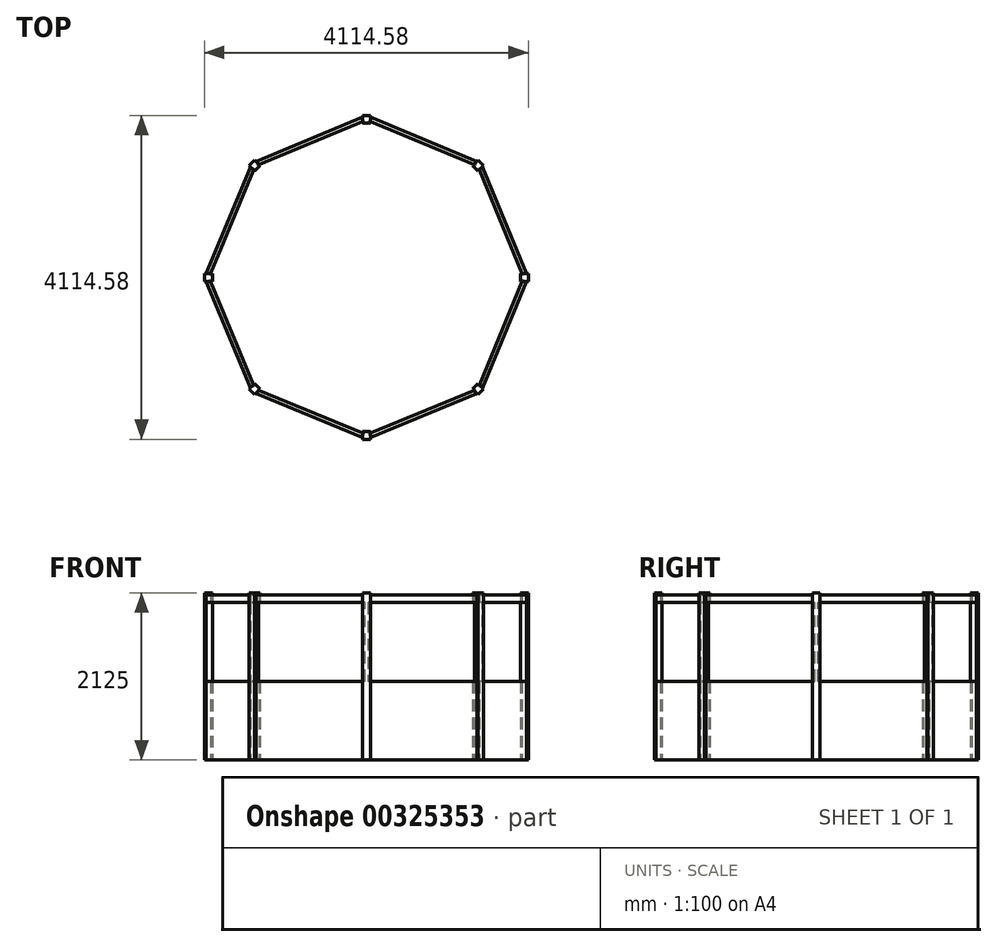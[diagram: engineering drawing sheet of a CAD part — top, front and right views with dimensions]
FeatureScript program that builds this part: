
annotation { "Feature Type Name" : "Feature", "Feature Type Description" : "" }
export const myFeature = defineFeature(function(context is Context, id is Id, definition is map)
    precondition{}
    {
        {
            var Q0;
            Q0=qCreatedBy(makeId("Top.planeOp"),FACE);
            var sketch = newSketch(context, id + "F0", { "sketchPlane" : qUnion([Q0])});
            skCircle(sketch, "E0.cCircle", {"center": v(0, 0) * mm, "radius": 1847.76 * mm, "construction": true});
            skLineSegment(sketch, "E0.0", {"start": v(2000, 0) * mm, "end": v(1414.21, -1414.21) * mm});
            skLineSegment(sketch, "E0.1", {"start": v(1414.21, -1414.21) * mm, "end": v(0, -2000) * mm});
            skLineSegment(sketch, "E0.2", {"start": v(0, -2000) * mm, "end": v(-1414.21, -1414.21) * mm});
            skLineSegment(sketch, "E0.3", {"start": v(-1414.21, -1414.21) * mm, "end": v(-2000, 0) * mm});
            skLineSegment(sketch, "E0.4", {"start": v(-2000, 0) * mm, "end": v(-1414.21, 1414.21) * mm});
            skLineSegment(sketch, "E0.5", {"start": v(-1414.21, 1414.21) * mm, "end": v(0, 2000) * mm});
            skLineSegment(sketch, "E0.6", {"start": v(0, 2000) * mm, "end": v(1414.21, 1414.21) * mm});
            skLineSegment(sketch, "E0.7", {"start": v(1414.21, 1414.21) * mm, "end": v(2000, 0) * mm});
            skPoint(sketch, "E0.0.midPoint", {"position": v(1707.1, -707.1) * mm});
            skPoint(sketch, "E1.middle", {"position": v(1414.21, -1414.21) * mm});
            skPoint(sketch, "E2.middle", {"position": v(2000, 0) * mm});
            skLineSegment(sketch, "E3", {"start": v(2017.31, -91.48) * mm, "end": v(2055.2, 0) * mm});
            skPoint(sketch, "E4.end.orphan", {"position": v(1956.9, 0) * mm});
            skPoint(sketch, "E5.end.orphan", {"position": v(2050, 0) * mm});
            skLineSegment(sketch, "E6.0", {"start": v(-1453.25, 1453.25) * mm, "end": v(0, 2055.2) * mm});
            skLineSegment(sketch, "E6.1", {"start": v(-2055.2, 0) * mm, "end": v(-1453.25, 1453.25) * mm});
            skLineSegment(sketch, "E6.2", {"start": v(0, 2055.2) * mm, "end": v(1453.25, 1453.25) * mm});
            skLineSegment(sketch, "E6.3", {"start": v(-1453.25, -1453.25) * mm, "end": v(-2055.2, 0) * mm});
            skLineSegment(sketch, "E6.4", {"start": v(1453.25, 1453.25) * mm, "end": v(2055.2, 0) * mm});
            skLineSegment(sketch, "E6.5", {"start": v(2055.2, 0) * mm, "end": v(1453.25, -1453.25) * mm});
            skLineSegment(sketch, "E6.6", {"start": v(1453.25, -1453.25) * mm, "end": v(0, -2055.2) * mm});
            skLineSegment(sketch, "E6.7", {"start": v(0, -2055.2) * mm, "end": v(-1453.25, -1453.25) * mm});
            skLineSegment(sketch, "E7", {"start": v(0, 2754.8) * mm, "end": v(0, -3839.53) * mm});
            skLineSegment(sketch, "E8", {"start": v(-2590.03, 0) * mm, "end": v(5183.87, 0) * mm});
            skLineSegment(sketch, "E9", {"start": v(2000, 0) * mm, "end": v(0, -2000) * mm});
            skLineSegment(sketch, "E10", {"start": v(0, 0) * mm, "end": v(1464.21, -1464.21) * mm});
            skLineSegment(sketch, "E11", {"start": v(0, -2055.2) * mm, "end": v(0, -2000) * mm});
            skPoint(sketch, "E12.middle", {"position": v(0, -2027.6) * mm});
            skLineSegment(sketch, "E13", {"start": v(-50, -1957.29) * mm, "end": v(-50, -2057.29) * mm});
            skLineSegment(sketch, "E14", {"start": v(50, -1957.29) * mm, "end": v(50, -2057.29) * mm});
            skLineSegment(sketch, "E15", {"start": v(-50, -1957.29) * mm, "end": v(50, -1957.29) * mm});
            skLineSegment(sketch, "E16", {"start": v(-50, -2057.29) * mm, "end": v(50, -2057.29) * mm});
            skLineSegment(sketch, "E17", {"start": v(-50, -1979.29) * mm, "end": v(50, -1979.29) * mm});
            skPoint(sketch, "E18.endSnap0", {"position": v(0, -1979.29) * mm});
            skLineSegment(sketch, "E19", {"start": v(-50, -2034.5) * mm, "end": v(50, -2034.5) * mm});
            skPoint(sketch, "E20.orphan", {"position": v(-81.67, -1979.29) * mm});
            skPoint(sketch, "E21.orphan", {"position": v(96.93, -1979.29) * mm});
            skLineSegment(sketch, "E22.1.0", {"start": v(1348.66, -1419.37) * mm, "end": v(1419.37, -1348.66) * mm});
            skLineSegment(sketch, "E22.1.1", {"start": v(1419.37, -1348.66) * mm, "end": v(1490.08, -1419.37) * mm});
            skLineSegment(sketch, "E22.1.2", {"start": v(1419.37, -1490.08) * mm, "end": v(1490.08, -1419.37) * mm});
            skLineSegment(sketch, "E22.1.3", {"start": v(1348.66, -1419.37) * mm, "end": v(1419.37, -1490.08) * mm});
            skLineSegment(sketch, "E22.anchor1", {"start": v(0, 0) * mm, "end": v(-50, -1957.29) * mm, "construction": true});
            skLineSegment(sketch, "E22.anchor2", {"start": v(0, 0) * mm, "end": v(-1419.37, -1348.66) * mm, "construction": true});
            skLineSegment(sketch, "E23.1.2.0", {"start": v(1957.29, -50) * mm, "end": v(1957.29, 50) * mm});
            skLineSegment(sketch, "E23.3.2.0", {"start": v(1957.29, 50) * mm, "end": v(2057.29, 50) * mm});
            skLineSegment(sketch, "E23.6.2.0", {"start": v(2057.29, -50) * mm, "end": v(2057.29, 50) * mm});
            skLineSegment(sketch, "E23.9.2.0", {"start": v(1957.29, -50) * mm, "end": v(2057.29, -50) * mm});
            skLineSegment(sketch, "E23.1.3.0", {"start": v(1419.37, 1348.66) * mm, "end": v(1348.66, 1419.37) * mm});
            skLineSegment(sketch, "E23.3.3.0", {"start": v(1348.66, 1419.37) * mm, "end": v(1419.37, 1490.08) * mm});
            skLineSegment(sketch, "E23.6.3.0", {"start": v(1490.08, 1419.37) * mm, "end": v(1419.37, 1490.08) * mm});
            skLineSegment(sketch, "E23.9.3.0", {"start": v(1419.37, 1348.66) * mm, "end": v(1490.08, 1419.37) * mm});
            skLineSegment(sketch, "E23.1.4.0", {"start": v(50, 1957.29) * mm, "end": v(-50, 1957.29) * mm});
            skLineSegment(sketch, "E23.3.4.0", {"start": v(-50, 1957.29) * mm, "end": v(-50, 2057.29) * mm});
            skLineSegment(sketch, "E23.6.4.0", {"start": v(50, 2057.29) * mm, "end": v(-50, 2057.29) * mm});
            skLineSegment(sketch, "E23.9.4.0", {"start": v(50, 1957.29) * mm, "end": v(50, 2057.29) * mm});
            skLineSegment(sketch, "E23.1.5.0", {"start": v(-1348.66, 1419.37) * mm, "end": v(-1419.37, 1348.66) * mm});
            skLineSegment(sketch, "E23.3.5.0", {"start": v(-1419.37, 1348.66) * mm, "end": v(-1490.08, 1419.37) * mm});
            skLineSegment(sketch, "E23.6.5.0", {"start": v(-1419.37, 1490.08) * mm, "end": v(-1490.08, 1419.37) * mm});
            skLineSegment(sketch, "E23.9.5.0", {"start": v(-1348.66, 1419.37) * mm, "end": v(-1419.37, 1490.08) * mm});
            skLineSegment(sketch, "E23.1.6.0", {"start": v(-1957.29, 50) * mm, "end": v(-1957.29, -50) * mm});
            skLineSegment(sketch, "E23.3.6.0", {"start": v(-1957.29, -50) * mm, "end": v(-2057.29, -50) * mm});
            skLineSegment(sketch, "E23.6.6.0", {"start": v(-2057.29, 50) * mm, "end": v(-2057.29, -50) * mm});
            skLineSegment(sketch, "E23.9.6.0", {"start": v(-1957.29, 50) * mm, "end": v(-2057.29, 50) * mm});
            skLineSegment(sketch, "E23.1.7.0", {"start": v(-1419.37, -1348.66) * mm, "end": v(-1348.66, -1419.37) * mm});
            skLineSegment(sketch, "E23.3.7.0", {"start": v(-1348.66, -1419.37) * mm, "end": v(-1419.37, -1490.08) * mm});
            skLineSegment(sketch, "E23.6.7.0", {"start": v(-1490.08, -1419.37) * mm, "end": v(-1419.37, -1490.08) * mm});
            skLineSegment(sketch, "E23.9.7.0", {"start": v(-1419.37, -1348.66) * mm, "end": v(-1490.08, -1419.37) * mm});
            skSolve(sketch);
        }
        {
            var Q0;
            {var subQ3=sQuery(id+"F0.wireOp",EDGE,"E14");var subQ5=sQuery(id+"F0.wireOp",EDGE,"E16");var subQ7=makeQuery(id+"F0.imprint","INTERSECT",VERTEX,{"derivedFrom":[subQ3,subQ5]});Q0=makeQuery(id+"F0.imprint","IMPRINT",FACE,{"disambiguationData":[TD([[makeQuery(id+"F0.imprint","IMPRINT",EDGE,{"disambiguationData":[TD([[subQ7,1.0]])],"derivedFrom":subQ5}),1.0]])]});}
            var Q1;
            {var subQ0=sQuery(id+"F0.wireOp",EDGE,"E11");var subQ3=sQuery(id+"F0.wireOp",EDGE,"E19");var subQ5=makeQuery(id+"F0.imprint","INTERSECT",VERTEX,{"derivedFrom":[subQ0,subQ3]});Q1=makeQuery(id+"F0.imprint","IMPRINT",FACE,{"disambiguationData":[TD([[makeQuery(id+"F0.imprint","IMPRINT",EDGE,{"disambiguationData":[TD([[subQ5,-1.0]])],"derivedFrom":subQ3}),-1.0]])]});}
            var Q2;
            {var subQ0=sQuery(id+"F0.wireOp",EDGE,"E11");var subQ3=sQuery(id+"F0.wireOp",EDGE,"E19");var subQ5=makeQuery(id+"F0.imprint","INTERSECT",VERTEX,{"derivedFrom":[subQ0,subQ3]});Q2=makeQuery(id+"F0.imprint","IMPRINT",FACE,{"disambiguationData":[TD([[makeQuery(id+"F0.imprint","IMPRINT",EDGE,{"disambiguationData":[TD([[subQ5,1.0]])],"derivedFrom":subQ3}),-1.0]])]});}
            var Q3;
            {var subQ3=sQuery(id+"F0.wireOp",EDGE,"E13");var subQ5=sQuery(id+"F0.wireOp",EDGE,"E16");var subQ7=makeQuery(id+"F0.imprint","INTERSECT",VERTEX,{"derivedFrom":[subQ3,subQ5]});Q3=makeQuery(id+"F0.imprint","IMPRINT",FACE,{"disambiguationData":[TD([[makeQuery(id+"F0.imprint","IMPRINT",EDGE,{"disambiguationData":[TD([[subQ7,-1.0]])],"derivedFrom":subQ5}),1.0]])]});}
            var Q4;
            {var subQ0=sQuery(id+"F0.wireOp",EDGE,"E11");var subQ5=sQuery(id+"F0.wireOp",EDGE,"E19");var subQ6=makeQuery(id+"F0.imprint","INTERSECT",VERTEX,{"derivedFrom":[subQ0,subQ5]});Q4=makeQuery(id+"F0.imprint","IMPRINT",FACE,{"disambiguationData":[TD([[makeQuery(id+"F0.imprint","IMPRINT",EDGE,{"disambiguationData":[TD([[subQ6,1.0]])],"derivedFrom":subQ5}),1.0]])]});}
            var Q5;
            {var subQ0=sQuery(id+"F0.wireOp",EDGE,"E11");var subQ5=sQuery(id+"F0.wireOp",EDGE,"E19");var subQ6=makeQuery(id+"F0.imprint","INTERSECT",VERTEX,{"derivedFrom":[subQ0,subQ5]});Q5=makeQuery(id+"F0.imprint","IMPRINT",FACE,{"disambiguationData":[TD([[makeQuery(id+"F0.imprint","IMPRINT",EDGE,{"disambiguationData":[TD([[subQ6,-1.0]])],"derivedFrom":subQ5}),1.0]])]});}
            var Q6;
            {var subQ0=sQuery(id+"F0.wireOp",EDGE,"E9");var subQ3=sQuery(id+"F0.wireOp",EDGE,"E17");var subQ5=makeQuery(id+"F0.imprint","INTERSECT",VERTEX,{"derivedFrom":[subQ0,subQ3]});Q6=makeQuery(id+"F0.imprint","IMPRINT",FACE,{"disambiguationData":[TD([[makeQuery(id+"F0.imprint","IMPRINT",EDGE,{"disambiguationData":[TD([[subQ5,-1.0]])],"derivedFrom":subQ3}),-1.0]])]});}
            var Q7;
            {var subQ1=sQuery(id+"F0.wireOp",EDGE,"E7");var subQ3=sQuery(id+"F0.wireOp",EDGE,"E17");var subQ4=makeQuery(id+"F0.imprint","INTERSECT",VERTEX,{"derivedFrom":[subQ1,subQ3]});Q7=makeQuery(id+"F0.imprint","IMPRINT",FACE,{"disambiguationData":[TD([[makeQuery(id+"F0.imprint","IMPRINT",EDGE,{"disambiguationData":[TD([[subQ4,-1.0]])],"derivedFrom":subQ3}),-1.0]])]});}
            var Q8;
            {var subQ0=sQuery(id+"F0.wireOp",EDGE,"E7");var subQ3=sQuery(id+"F0.wireOp",EDGE,"E17");var subQ5=makeQuery(id+"F0.imprint","INTERSECT",VERTEX,{"derivedFrom":[subQ0,subQ3]});Q8=makeQuery(id+"F0.imprint","IMPRINT",FACE,{"disambiguationData":[TD([[makeQuery(id+"F0.imprint","IMPRINT",EDGE,{"disambiguationData":[TD([[subQ5,1.0]])],"derivedFrom":subQ3}),-1.0]])]});}
            var Q9;
            {var subQ0=sQuery(id+"F0.wireOp",EDGE,"E15");var subQ1=sQuery(id+"F0.wireOp",EDGE,"E7");var subQ2=makeQuery(id+"F0.imprint","INTERSECT",VERTEX,{"derivedFrom":[subQ1,subQ0]});Q9=makeQuery(id+"F0.imprint","IMPRINT",FACE,{"disambiguationData":[TD([[makeQuery(id+"F0.imprint","IMPRINT",EDGE,{"disambiguationData":[TD([[subQ2,-1.0]])],"derivedFrom":subQ1}),-1.0]])]});}
            var Q10;
            {var subQ0=sQuery(id+"F0.wireOp",EDGE,"E15");var subQ1=sQuery(id+"F0.wireOp",EDGE,"E7");var subQ2=makeQuery(id+"F0.imprint","INTERSECT",VERTEX,{"derivedFrom":[subQ1,subQ0]});Q10=makeQuery(id+"F0.imprint","IMPRINT",FACE,{"disambiguationData":[TD([[makeQuery(id+"F0.imprint","IMPRINT",EDGE,{"disambiguationData":[TD([[subQ2,-1.0]])],"derivedFrom":subQ1}),1.0]])]});}
            var Q11;
            {var subQ0=sQuery(id+"F0.wireOp",EDGE,"E15");var subQ1=sQuery(id+"F0.wireOp",EDGE,"E9");var subQ2=makeQuery(id+"F0.imprint","INTERSECT",VERTEX,{"derivedFrom":[subQ1,subQ0]});Q11=makeQuery(id+"F0.imprint","IMPRINT",FACE,{"disambiguationData":[TD([[makeQuery(id+"F0.imprint","IMPRINT",EDGE,{"disambiguationData":[TD([[subQ2,-1.0]])],"derivedFrom":subQ1}),1.0]])]});}
            var Q12;
            {var subQ0=sQuery(id+"F0.wireOp",EDGE,"E23.6.7.0");Q12=makeQuery(id+"F0.imprint","IMPRINT",FACE,{"disambiguationData":[TD([[makeQuery(id+"F0.imprint","IMPRINT",EDGE,{"derivedFrom":subQ0}),1.0]])]});}
            var Q13;
            {var subQ5=sQuery(id+"F0.wireOp",EDGE,"E0.3");var subQ6=sQuery(id+"F0.wireOp",EDGE,"E0.2");var subQ7=makeQuery(id+"F0.imprint","INTERSECT",VERTEX,{"derivedFrom":[subQ6,subQ5]});Q13=makeQuery(id+"F0.imprint","IMPRINT",FACE,{"disambiguationData":[TD([[makeQuery(id+"F0.imprint","IMPRINT",EDGE,{"disambiguationData":[TD([[subQ7,1.0]])],"derivedFrom":subQ6}),1.0]])]});}
            var Q14;
            {var subQ1=sQuery(id+"F0.wireOp",EDGE,"E23.1.7.0");Q14=makeQuery(id+"F0.imprint","IMPRINT",FACE,{"disambiguationData":[TD([[makeQuery(id+"F0.imprint","IMPRINT",EDGE,{"derivedFrom":subQ1}),-1.0]])]});}
            var Q15;
            {var subQ3=sQuery(id+"F0.wireOp",EDGE,"E23.3.6.0");var subQ5=sQuery(id+"F0.wireOp",EDGE,"E6.3");var subQ7=makeQuery(id+"F0.imprint","INTERSECT",VERTEX,{"derivedFrom":[subQ5,subQ3]});Q15=makeQuery(id+"F0.imprint","IMPRINT",FACE,{"disambiguationData":[TD([[makeQuery(id+"F0.imprint","IMPRINT",EDGE,{"disambiguationData":[TD([[subQ7,1.0]])],"derivedFrom":subQ3}),-1.0]])]});}
            var Q16;
            {var subQ3=sQuery(id+"F0.wireOp",EDGE,"E23.3.6.0");var subQ5=sQuery(id+"F0.wireOp",EDGE,"E23.6.6.0");var subQ6=makeQuery(id+"F0.imprint","INTERSECT",VERTEX,{"derivedFrom":[subQ3,subQ5]});Q16=makeQuery(id+"F0.imprint","IMPRINT",FACE,{"disambiguationData":[TD([[makeQuery(id+"F0.imprint","IMPRINT",EDGE,{"disambiguationData":[TD([[subQ6,1.0]])],"derivedFrom":subQ3}),-1.0]])]});}
            var Q17;
            {var subQ3=sQuery(id+"F0.wireOp",EDGE,"E23.9.6.0");var subQ5=sQuery(id+"F0.wireOp",EDGE,"E23.6.6.0");var subQ7=makeQuery(id+"F0.imprint","INTERSECT",VERTEX,{"derivedFrom":[subQ5,subQ3]});Q17=makeQuery(id+"F0.imprint","IMPRINT",FACE,{"disambiguationData":[TD([[makeQuery(id+"F0.imprint","IMPRINT",EDGE,{"disambiguationData":[TD([[subQ7,-1.0]])],"derivedFrom":subQ5}),1.0]])]});}
            var Q18;
            {var subQ3=sQuery(id+"F0.wireOp",EDGE,"E23.9.6.0");var subQ5=sQuery(id+"F0.wireOp",EDGE,"E6.1");var subQ7=makeQuery(id+"F0.imprint","INTERSECT",VERTEX,{"derivedFrom":[subQ5,subQ3]});Q18=makeQuery(id+"F0.imprint","IMPRINT",FACE,{"disambiguationData":[TD([[makeQuery(id+"F0.imprint","IMPRINT",EDGE,{"disambiguationData":[TD([[subQ7,1.0]])],"derivedFrom":subQ3}),1.0]])]});}
            var Q19;
            {var subQ3=sQuery(id+"F0.wireOp",EDGE,"E23.9.6.0");var subQ5=sQuery(id+"F0.wireOp",EDGE,"E23.1.6.0");var subQ7=makeQuery(id+"F0.imprint","INTERSECT",VERTEX,{"derivedFrom":[subQ5,subQ3]});Q19=makeQuery(id+"F0.imprint","IMPRINT",FACE,{"disambiguationData":[TD([[makeQuery(id+"F0.imprint","IMPRINT",EDGE,{"disambiguationData":[TD([[subQ7,-1.0]])],"derivedFrom":subQ5}),-1.0]])]});}
            var Q20;
            {var subQ3=sQuery(id+"F0.wireOp",EDGE,"E23.3.6.0");var subQ5=sQuery(id+"F0.wireOp",EDGE,"E23.1.6.0");var subQ6=makeQuery(id+"F0.imprint","INTERSECT",VERTEX,{"derivedFrom":[subQ5,subQ3]});Q20=makeQuery(id+"F0.imprint","IMPRINT",FACE,{"disambiguationData":[TD([[makeQuery(id+"F0.imprint","IMPRINT",EDGE,{"disambiguationData":[TD([[subQ6,1.0]])],"derivedFrom":subQ5}),-1.0]])]});}
            var Q21;
            {var subQ1=sQuery(id+"F0.wireOp",EDGE,"E23.1.5.0");Q21=makeQuery(id+"F0.imprint","IMPRINT",FACE,{"disambiguationData":[TD([[makeQuery(id+"F0.imprint","IMPRINT",EDGE,{"derivedFrom":subQ1}),-1.0]])]});}
            var Q22;
            {var subQ0=sQuery(id+"F0.wireOp",EDGE,"E0.5");var subQ1=sQuery(id+"F0.wireOp",EDGE,"E0.4");var subQ2=makeQuery(id+"F0.imprint","INTERSECT",VERTEX,{"derivedFrom":[subQ1,subQ0]});Q22=makeQuery(id+"F0.imprint","IMPRINT",FACE,{"disambiguationData":[TD([[makeQuery(id+"F0.imprint","IMPRINT",EDGE,{"disambiguationData":[TD([[subQ2,1.0]])],"derivedFrom":subQ1}),1.0]])]});}
            var Q23;
            {var subQ0=sQuery(id+"F0.wireOp",EDGE,"E23.6.5.0");Q23=makeQuery(id+"F0.imprint","IMPRINT",FACE,{"disambiguationData":[TD([[makeQuery(id+"F0.imprint","IMPRINT",EDGE,{"derivedFrom":subQ0}),1.0]])]});}
            var Q24;
            {var subQ3=sQuery(id+"F0.wireOp",EDGE,"E23.9.4.0");var subQ5=sQuery(id+"F0.wireOp",EDGE,"E23.1.4.0");var subQ6=makeQuery(id+"F0.imprint","INTERSECT",VERTEX,{"derivedFrom":[subQ5,subQ3]});Q24=makeQuery(id+"F0.imprint","IMPRINT",FACE,{"disambiguationData":[TD([[makeQuery(id+"F0.imprint","IMPRINT",EDGE,{"disambiguationData":[TD([[subQ6,-1.0]])],"derivedFrom":subQ5}),-1.0]])]});}
            var Q25;
            {var subQ3=sQuery(id+"F0.wireOp",EDGE,"E23.3.4.0");var subQ5=sQuery(id+"F0.wireOp",EDGE,"E23.1.4.0");var subQ6=makeQuery(id+"F0.imprint","INTERSECT",VERTEX,{"derivedFrom":[subQ5,subQ3]});Q25=makeQuery(id+"F0.imprint","IMPRINT",FACE,{"disambiguationData":[TD([[makeQuery(id+"F0.imprint","IMPRINT",EDGE,{"disambiguationData":[TD([[subQ6,1.0]])],"derivedFrom":subQ5}),-1.0]])]});}
            var Q26;
            {var subQ3=sQuery(id+"F0.wireOp",EDGE,"E23.3.4.0");var subQ5=sQuery(id+"F0.wireOp",EDGE,"E6.0");var subQ7=makeQuery(id+"F0.imprint","INTERSECT",VERTEX,{"derivedFrom":[subQ5,subQ3]});Q26=makeQuery(id+"F0.imprint","IMPRINT",FACE,{"disambiguationData":[TD([[makeQuery(id+"F0.imprint","IMPRINT",EDGE,{"disambiguationData":[TD([[subQ7,1.0]])],"derivedFrom":subQ3}),-1.0]])]});}
            var Q27;
            {var subQ3=sQuery(id+"F0.wireOp",EDGE,"E23.9.4.0");var subQ5=sQuery(id+"F0.wireOp",EDGE,"E6.2");var subQ7=makeQuery(id+"F0.imprint","INTERSECT",VERTEX,{"derivedFrom":[subQ5,subQ3]});Q27=makeQuery(id+"F0.imprint","IMPRINT",FACE,{"disambiguationData":[TD([[makeQuery(id+"F0.imprint","IMPRINT",EDGE,{"disambiguationData":[TD([[subQ7,1.0]])],"derivedFrom":subQ3}),1.0]])]});}
            var Q28;
            {var subQ3=sQuery(id+"F0.wireOp",EDGE,"E23.9.4.0");var subQ5=sQuery(id+"F0.wireOp",EDGE,"E23.6.4.0");var subQ6=makeQuery(id+"F0.imprint","INTERSECT",VERTEX,{"derivedFrom":[subQ5,subQ3]});Q28=makeQuery(id+"F0.imprint","IMPRINT",FACE,{"disambiguationData":[TD([[makeQuery(id+"F0.imprint","IMPRINT",EDGE,{"disambiguationData":[TD([[subQ6,-1.0]])],"derivedFrom":subQ5}),1.0]])]});}
            var Q29;
            {var subQ3=sQuery(id+"F0.wireOp",EDGE,"E23.3.4.0");var subQ5=sQuery(id+"F0.wireOp",EDGE,"E23.6.4.0");var subQ7=makeQuery(id+"F0.imprint","INTERSECT",VERTEX,{"derivedFrom":[subQ3,subQ5]});Q29=makeQuery(id+"F0.imprint","IMPRINT",FACE,{"disambiguationData":[TD([[makeQuery(id+"F0.imprint","IMPRINT",EDGE,{"disambiguationData":[TD([[subQ7,1.0]])],"derivedFrom":subQ3}),-1.0]])]});}
            var Q30;
            {var subQ0=sQuery(id+"F0.wireOp",EDGE,"E23.6.3.0");Q30=makeQuery(id+"F0.imprint","IMPRINT",FACE,{"disambiguationData":[TD([[makeQuery(id+"F0.imprint","IMPRINT",EDGE,{"derivedFrom":subQ0}),1.0]])]});}
            var Q31;
            {var subQ5=sQuery(id+"F0.wireOp",EDGE,"E0.7");var subQ6=sQuery(id+"F0.wireOp",EDGE,"E0.6");var subQ7=makeQuery(id+"F0.imprint","INTERSECT",VERTEX,{"derivedFrom":[subQ6,subQ5]});Q31=makeQuery(id+"F0.imprint","IMPRINT",FACE,{"disambiguationData":[TD([[makeQuery(id+"F0.imprint","IMPRINT",EDGE,{"disambiguationData":[TD([[subQ7,1.0]])],"derivedFrom":subQ6}),1.0]])]});}
            var Q32;
            {var subQ1=sQuery(id+"F0.wireOp",EDGE,"E23.1.3.0");Q32=makeQuery(id+"F0.imprint","IMPRINT",FACE,{"disambiguationData":[TD([[makeQuery(id+"F0.imprint","IMPRINT",EDGE,{"derivedFrom":subQ1}),-1.0]])]});}
            var Q33;
            {var subQ3=sQuery(id+"F0.wireOp",EDGE,"E23.9.2.0");var subQ5=sQuery(id+"F0.wireOp",EDGE,"E6.5");var subQ7=makeQuery(id+"F0.imprint","INTERSECT",VERTEX,{"derivedFrom":[subQ5,subQ3]});Q33=makeQuery(id+"F0.imprint","IMPRINT",FACE,{"disambiguationData":[TD([[makeQuery(id+"F0.imprint","IMPRINT",EDGE,{"disambiguationData":[TD([[subQ7,1.0]])],"derivedFrom":subQ3}),1.0]])]});}
            var Q34;
            {var subQ3=sQuery(id+"F0.wireOp",EDGE,"E23.3.2.0");var subQ5=sQuery(id+"F0.wireOp",EDGE,"E6.4");var subQ7=makeQuery(id+"F0.imprint","INTERSECT",VERTEX,{"derivedFrom":[subQ5,subQ3]});Q34=makeQuery(id+"F0.imprint","IMPRINT",FACE,{"disambiguationData":[TD([[makeQuery(id+"F0.imprint","IMPRINT",EDGE,{"disambiguationData":[TD([[subQ7,1.0]])],"derivedFrom":subQ3}),-1.0]])]});}
            var Q35;
            {var subQ3=sQuery(id+"F0.wireOp",EDGE,"E23.3.2.0");var subQ5=sQuery(id+"F0.wireOp",EDGE,"E23.1.2.0");var subQ7=makeQuery(id+"F0.imprint","INTERSECT",VERTEX,{"derivedFrom":[subQ5,subQ3]});Q35=makeQuery(id+"F0.imprint","IMPRINT",FACE,{"disambiguationData":[TD([[makeQuery(id+"F0.imprint","IMPRINT",EDGE,{"disambiguationData":[TD([[subQ7,1.0]])],"derivedFrom":subQ5}),-1.0]])]});}
            var Q36;
            {var subQ1=sQuery(id+"F0.wireOp",EDGE,"E8");var subQ3=sQuery(id+"F0.wireOp",EDGE,"E23.1.2.0");var subQ4=makeQuery(id+"F0.imprint","INTERSECT",VERTEX,{"derivedFrom":[subQ1,subQ3]});Q36=makeQuery(id+"F0.imprint","IMPRINT",FACE,{"disambiguationData":[TD([[makeQuery(id+"F0.imprint","IMPRINT",EDGE,{"disambiguationData":[TD([[subQ4,1.0]])],"derivedFrom":subQ3}),-1.0]])]});}
            var Q37;
            {var subQ3=sQuery(id+"F0.wireOp",EDGE,"E23.9.2.0");var subQ5=sQuery(id+"F0.wireOp",EDGE,"E23.1.2.0");var subQ6=makeQuery(id+"F0.imprint","INTERSECT",VERTEX,{"derivedFrom":[subQ5,subQ3]});Q37=makeQuery(id+"F0.imprint","IMPRINT",FACE,{"disambiguationData":[TD([[makeQuery(id+"F0.imprint","IMPRINT",EDGE,{"disambiguationData":[TD([[subQ6,-1.0]])],"derivedFrom":subQ5}),-1.0]])]});}
            var Q38;
            {var subQ3=sQuery(id+"F0.wireOp",EDGE,"E23.9.2.0");var subQ5=sQuery(id+"F0.wireOp",EDGE,"E23.6.2.0");var subQ7=makeQuery(id+"F0.imprint","INTERSECT",VERTEX,{"derivedFrom":[subQ5,subQ3]});Q38=makeQuery(id+"F0.imprint","IMPRINT",FACE,{"disambiguationData":[TD([[makeQuery(id+"F0.imprint","IMPRINT",EDGE,{"disambiguationData":[TD([[subQ7,-1.0]])],"derivedFrom":subQ5}),1.0]])]});}
            var Q39;
            {var subQ3=sQuery(id+"F0.wireOp",EDGE,"E23.3.2.0");var subQ5=sQuery(id+"F0.wireOp",EDGE,"E23.6.2.0");var subQ7=makeQuery(id+"F0.imprint","INTERSECT",VERTEX,{"derivedFrom":[subQ3,subQ5]});Q39=makeQuery(id+"F0.imprint","IMPRINT",FACE,{"disambiguationData":[TD([[makeQuery(id+"F0.imprint","IMPRINT",EDGE,{"disambiguationData":[TD([[subQ7,1.0]])],"derivedFrom":subQ3}),-1.0]])]});}
            var Q40;
            {var subQ3=sQuery(id+"F0.wireOp",EDGE,"E22.1.3");var subQ5=sQuery(id+"F0.wireOp",EDGE,"E6.6");var subQ7=makeQuery(id+"F0.imprint","INTERSECT",VERTEX,{"derivedFrom":[subQ5,subQ3]});Q40=makeQuery(id+"F0.imprint","IMPRINT",FACE,{"disambiguationData":[TD([[makeQuery(id+"F0.imprint","IMPRINT",EDGE,{"disambiguationData":[TD([[subQ7,1.0]])],"derivedFrom":subQ3}),1.0]])]});}
            var Q41;
            {var subQ3=sQuery(id+"F0.wireOp",EDGE,"E22.1.1");var subQ5=sQuery(id+"F0.wireOp",EDGE,"E6.5");var subQ7=makeQuery(id+"F0.imprint","INTERSECT",VERTEX,{"derivedFrom":[subQ5,subQ3]});Q41=makeQuery(id+"F0.imprint","IMPRINT",FACE,{"disambiguationData":[TD([[makeQuery(id+"F0.imprint","IMPRINT",EDGE,{"disambiguationData":[TD([[subQ7,1.0]])],"derivedFrom":subQ3}),-1.0]])]});}
            var Q42;
            {var subQ3=sQuery(id+"F0.wireOp",EDGE,"E22.1.1");var subQ5=sQuery(id+"F0.wireOp",EDGE,"E22.1.2");var subQ6=makeQuery(id+"F0.imprint","INTERSECT",VERTEX,{"derivedFrom":[subQ3,subQ5]});Q42=makeQuery(id+"F0.imprint","IMPRINT",FACE,{"disambiguationData":[TD([[makeQuery(id+"F0.imprint","IMPRINT",EDGE,{"disambiguationData":[TD([[subQ6,1.0]])],"derivedFrom":subQ3}),-1.0]])]});}
            var Q43;
            {var subQ3=sQuery(id+"F0.wireOp",EDGE,"E22.1.3");var subQ5=sQuery(id+"F0.wireOp",EDGE,"E22.1.2");var subQ6=makeQuery(id+"F0.imprint","INTERSECT",VERTEX,{"derivedFrom":[subQ5,subQ3]});Q43=makeQuery(id+"F0.imprint","IMPRINT",FACE,{"disambiguationData":[TD([[makeQuery(id+"F0.imprint","IMPRINT",EDGE,{"disambiguationData":[TD([[subQ6,-1.0]])],"derivedFrom":subQ5}),1.0]])]});}
            var Q44;
            {var subQ3=sQuery(id+"F0.wireOp",EDGE,"E22.1.3");var subQ5=sQuery(id+"F0.wireOp",EDGE,"E22.1.0");var subQ7=makeQuery(id+"F0.imprint","INTERSECT",VERTEX,{"derivedFrom":[subQ5,subQ3]});Q44=makeQuery(id+"F0.imprint","IMPRINT",FACE,{"disambiguationData":[TD([[makeQuery(id+"F0.imprint","IMPRINT",EDGE,{"disambiguationData":[TD([[subQ7,-1.0]])],"derivedFrom":subQ5}),-1.0]])]});}
            var Q45;
            {var subQ3=sQuery(id+"F0.wireOp",EDGE,"E22.1.1");var subQ5=sQuery(id+"F0.wireOp",EDGE,"E22.1.0");var subQ7=makeQuery(id+"F0.imprint","INTERSECT",VERTEX,{"derivedFrom":[subQ5,subQ3]});Q45=makeQuery(id+"F0.imprint","IMPRINT",FACE,{"disambiguationData":[TD([[makeQuery(id+"F0.imprint","IMPRINT",EDGE,{"disambiguationData":[TD([[subQ7,1.0]])],"derivedFrom":subQ5}),-1.0]])]});}
            extrude(context, id + "F1", {"entities" : qUnion([Q0, Q1, Q2, Q3, Q4, Q5, Q6, Q7, Q8, Q9, Q10, Q11, Q12, Q13, Q14, Q15, Q16, Q17, Q18, Q19, Q20, Q21, Q22, Q23, Q24, Q25, Q26, Q27, Q28, Q29, Q30, Q31, Q32, Q33, Q34, Q35, Q36, Q37, Q38, Q39, Q40, Q41, Q42, Q43, Q44, Q45]), "depth" : 2125 * mm});
        }
        {
            var Q0;
            {var subQ3=sQuery(id+"F0.wireOp",EDGE,"E22.1.3");var subQ5=sQuery(id+"F0.wireOp",EDGE,"E6.6");var subQ7=makeQuery(id+"F0.imprint","INTERSECT",VERTEX,{"derivedFrom":[subQ5,subQ3]});Q0=makeQuery(id+"F0.imprint","IMPRINT",FACE,{"disambiguationData":[TD([[makeQuery(id+"F0.imprint","IMPRINT",EDGE,{"disambiguationData":[TD([[subQ7,1.0]])],"derivedFrom":subQ3}),-1.0]])]});}
            var Q1;
            {var subQ0=sQuery(id+"F0.wireOp",EDGE,"E23.9.2.0");var subQ1=sQuery(id+"F0.wireOp",EDGE,"E0.0");var subQ2=makeQuery(id+"F0.imprint","INTERSECT",VERTEX,{"derivedFrom":[subQ1,subQ0]});Q1=makeQuery(id+"F0.imprint","IMPRINT",FACE,{"disambiguationData":[TD([[makeQuery(id+"F0.imprint","IMPRINT",EDGE,{"disambiguationData":[TD([[subQ2,-1.0]])],"derivedFrom":subQ1}),1.0]])]});}
            var Q2;
            {var subQ3=sQuery(id+"F0.wireOp",EDGE,"E23.3.7.0");var subQ5=sQuery(id+"F0.wireOp",EDGE,"E6.7");var subQ7=makeQuery(id+"F0.imprint","INTERSECT",VERTEX,{"derivedFrom":[subQ5,subQ3]});Q2=makeQuery(id+"F0.imprint","IMPRINT",FACE,{"disambiguationData":[TD([[makeQuery(id+"F0.imprint","IMPRINT",EDGE,{"disambiguationData":[TD([[subQ7,1.0]])],"derivedFrom":subQ3}),1.0]])]});}
            var Q3;
            {var subQ0=sQuery(id+"F0.wireOp",EDGE,"E23.9.7.0");var subQ1=sQuery(id+"F0.wireOp",EDGE,"E0.3");var subQ2=makeQuery(id+"F0.imprint","INTERSECT",VERTEX,{"derivedFrom":[subQ1,subQ0]});Q3=makeQuery(id+"F0.imprint","IMPRINT",FACE,{"disambiguationData":[TD([[makeQuery(id+"F0.imprint","IMPRINT",EDGE,{"disambiguationData":[TD([[subQ2,-1.0]])],"derivedFrom":subQ1}),1.0]])]});}
            var Q4;
            {var subQ0=sQuery(id+"F0.wireOp",EDGE,"E23.9.6.0");var subQ1=sQuery(id+"F0.wireOp",EDGE,"E0.4");var subQ2=makeQuery(id+"F0.imprint","INTERSECT",VERTEX,{"derivedFrom":[subQ1,subQ0]});Q4=makeQuery(id+"F0.imprint","IMPRINT",FACE,{"disambiguationData":[TD([[makeQuery(id+"F0.imprint","IMPRINT",EDGE,{"disambiguationData":[TD([[subQ2,-1.0]])],"derivedFrom":subQ1}),1.0]])]});}
            var Q5;
            {var subQ0=sQuery(id+"F0.wireOp",EDGE,"E23.9.5.0");var subQ1=sQuery(id+"F0.wireOp",EDGE,"E0.5");var subQ2=makeQuery(id+"F0.imprint","INTERSECT",VERTEX,{"derivedFrom":[subQ1,subQ0]});Q5=makeQuery(id+"F0.imprint","IMPRINT",FACE,{"disambiguationData":[TD([[makeQuery(id+"F0.imprint","IMPRINT",EDGE,{"disambiguationData":[TD([[subQ2,-1.0]])],"derivedFrom":subQ1}),1.0]])]});}
            var Q6;
            {var subQ0=sQuery(id+"F0.wireOp",EDGE,"E23.9.4.0");var subQ1=sQuery(id+"F0.wireOp",EDGE,"E0.6");var subQ2=makeQuery(id+"F0.imprint","INTERSECT",VERTEX,{"derivedFrom":[subQ1,subQ0]});Q6=makeQuery(id+"F0.imprint","IMPRINT",FACE,{"disambiguationData":[TD([[makeQuery(id+"F0.imprint","IMPRINT",EDGE,{"disambiguationData":[TD([[subQ2,-1.0]])],"derivedFrom":subQ1}),1.0]])]});}
            var Q7;
            {var subQ0=sQuery(id+"F0.wireOp",EDGE,"E23.9.3.0");var subQ1=sQuery(id+"F0.wireOp",EDGE,"E0.7");var subQ2=makeQuery(id+"F0.imprint","INTERSECT",VERTEX,{"derivedFrom":[subQ1,subQ0]});Q7=makeQuery(id+"F0.imprint","IMPRINT",FACE,{"disambiguationData":[TD([[makeQuery(id+"F0.imprint","IMPRINT",EDGE,{"disambiguationData":[TD([[subQ2,-1.0]])],"derivedFrom":subQ1}),1.0]])]});}
            extrude(context, id + "F2", {"entities" : qUnion([Q0, Q1, Q2, Q3, Q4, Q5, Q6, Q7]), "depth" : 2100 * mm});
        }
        {
            var Q0;
            Q0=makeQuery(id+"F2.opExtrude","SWEPT_FACE",FACE,{"disambiguationData":[OSD([sQuery(id+"F0.wireOp",EDGE,"E6.7")])]});
            var sketch = newSketch(context, id + "F3", { "sketchPlane" : qUnion([Q0])});
            skLineSegment(sketch, "E24.bottom", {"start": v(-732.37, 2000) * mm, "end": v(732.37, 2000) * mm});
            skLineSegment(sketch, "E24.top", {"start": v(-732.37, 1000) * mm, "end": v(732.37, 1000) * mm});
            skLineSegment(sketch, "E24.left", {"start": v(-732.37, 2000) * mm, "end": v(-732.37, 1000) * mm});
            skLineSegment(sketch, "E24.right", {"start": v(732.37, 2000) * mm, "end": v(732.37, 1000) * mm});
            skSolve(sketch);
        }
        {
            var Q0;
            Q0=makeQuery(id+"F3.imprint","IMPRINT",FACE,{"disambiguationData":[TD([[makeQuery(id+"F3.imprint","IMPRINT",EDGE,{"derivedFrom":sQuery(id+"F3.wireOp",EDGE,"E24.bottom")}),-1.0]])]});
            extrude(context, id + "F4", {"entities" : qUnion([Q0]), "operationType" : NewBodyOperationType.REMOVE, "oppositeDirection" : true, "depth" : 4000 * mm});
        }
        {
            var Q0;
            Q0=makeQuery(id+"F2.opExtrude","SWEPT_FACE",FACE,{"disambiguationData":[OSD([sQuery(id+"F0.wireOp",EDGE,"E6.3")])]});
            var sketch = newSketch(context, id + "F5", { "sketchPlane" : qUnion([Q0])});
            skLineSegment(sketch, "E25.bottom", {"start": v(-732.37, 2000) * mm, "end": v(732.37, 2000) * mm});
            skLineSegment(sketch, "E25.top", {"start": v(-732.37, 1000) * mm, "end": v(732.37, 1000) * mm});
            skLineSegment(sketch, "E25.left", {"start": v(-732.37, 2000) * mm, "end": v(-732.37, 1000) * mm});
            skLineSegment(sketch, "E25.right", {"start": v(732.37, 2000) * mm, "end": v(732.37, 1000) * mm});
            skSolve(sketch);
        }
        {
            var Q0;
            Q0=makeQuery(id+"F2.opExtrude","SWEPT_FACE",FACE,{"disambiguationData":[OSD([sQuery(id+"F0.wireOp",EDGE,"E6.1")])]});
            var sketch = newSketch(context, id + "F6", { "sketchPlane" : qUnion([Q0])});
            skLineSegment(sketch, "E26.bottom", {"start": v(-732.37, 2000) * mm, "end": v(732.37, 2000) * mm});
            skLineSegment(sketch, "E26.top", {"start": v(-732.37, 1000) * mm, "end": v(732.37, 1000) * mm});
            skLineSegment(sketch, "E26.left", {"start": v(-732.37, 2000) * mm, "end": v(-732.37, 1000) * mm});
            skLineSegment(sketch, "E26.right", {"start": v(732.37, 2000) * mm, "end": v(732.37, 1000) * mm});
            skSolve(sketch);
        }
        {
            var Q0;
            Q0=makeQuery(id+"F2.opExtrude","SWEPT_FACE",FACE,{"disambiguationData":[OSD([sQuery(id+"F0.wireOp",EDGE,"E6.0")])]});
            var sketch = newSketch(context, id + "F7", { "sketchPlane" : qUnion([Q0])});
            skLineSegment(sketch, "E27.bottom", {"start": v(-732.37, 2000) * mm, "end": v(732.37, 2000) * mm});
            skLineSegment(sketch, "E27.top", {"start": v(-732.37, 1000) * mm, "end": v(732.37, 1000) * mm});
            skLineSegment(sketch, "E27.left", {"start": v(-732.37, 2000) * mm, "end": v(-732.37, 1000) * mm});
            skLineSegment(sketch, "E27.right", {"start": v(732.37, 2000) * mm, "end": v(732.37, 1050) * mm});
            skSolve(sketch);
        }
        {
            var Q0;
            Q0=makeQuery(id+"F5.imprint","IMPRINT",FACE,{"disambiguationData":[TD([[makeQuery(id+"F5.imprint","IMPRINT",EDGE,{"derivedFrom":sQuery(id+"F5.wireOp",EDGE,"E25.bottom")}),-1.0]])]});
            extrude(context, id + "F8", {"entities" : qUnion([Q0]), "operationType" : NewBodyOperationType.REMOVE, "oppositeDirection" : true, "depth" : 4000 * mm});
        }
        {
            var Q0;
            Q0=makeQuery(id+"F6.imprint","IMPRINT",FACE,{"disambiguationData":[TD([[makeQuery(id+"F6.imprint","IMPRINT",EDGE,{"derivedFrom":sQuery(id+"F6.wireOp",EDGE,"E26.bottom")}),-1.0]])]});
            extrude(context, id + "F9", {"entities" : qUnion([Q0]), "operationType" : NewBodyOperationType.REMOVE, "oppositeDirection" : true, "depth" : 4000 * mm});
        }
        {
            var Q0;
            Q0=makeQuery(id+"F7.imprint","IMPRINT",FACE,{"disambiguationData":[TD([[makeQuery(id+"F7.imprint","IMPRINT",EDGE,{"derivedFrom":sQuery(id+"F7.wireOp",EDGE,"E27.bottom")}),-1.0]])]});
            extrude(context, id + "F10", {"entities" : qUnion([Q0]), "operationType" : NewBodyOperationType.REMOVE, "oppositeDirection" : true, "depth" : 4500 * mm});
        }
    });
